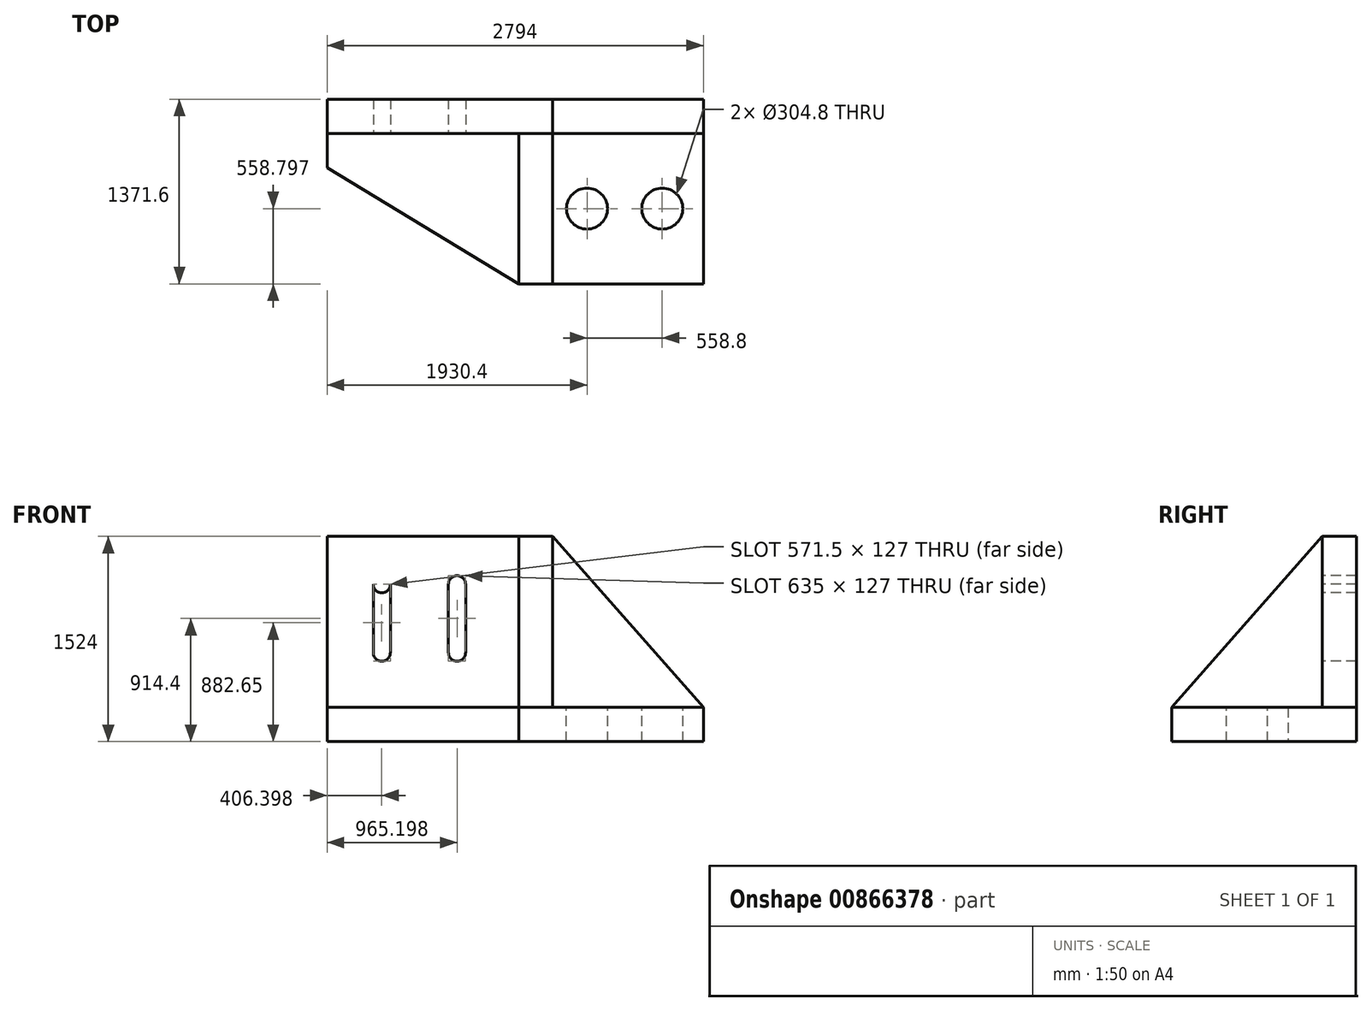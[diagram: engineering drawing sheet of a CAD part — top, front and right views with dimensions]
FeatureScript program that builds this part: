
annotation { "Feature Type Name" : "Feature", "Feature Type Description" : "" }
export const myFeature = defineFeature(function(context is Context, id is Id, definition is map)
    precondition{}
    {
        {
            var Q0;
            Q0=qCreatedBy(makeId("Top.planeOp"),FACE);
            var sketch = newSketch(context, id + "F0", { "sketchPlane" : qUnion([Q0])});
            skLineSegment(sketch, "E0", {"start": v(-275.52, -549.3) * mm, "end": v(1096.08, -549.3) * mm});
            skLineSegment(sketch, "E1", {"start": v(1096.08, -549.3) * mm, "end": v(1096.08, 822.3) * mm});
            skLineSegment(sketch, "E2", {"start": v(1096.08, 822.3) * mm, "end": v(-1697.92, 822.3) * mm});
            skLineSegment(sketch, "E3", {"start": v(-1697.92, 822.3) * mm, "end": v(-1697.92, 314.3) * mm});
            skLineSegment(sketch, "E4", {"start": v(-1697.92, 314.3) * mm, "end": v(-275.52, -549.3) * mm});
            skSolve(sketch);
        }
        {
            var Q0;
            Q0=makeQuery(id+"F0.imprint","IMPRINT",FACE,{"disambiguationData":[TD([[makeQuery(id+"F0.imprint","IMPRINT",EDGE,{"derivedFrom":sQuery(id+"F0.wireOp",EDGE,"E0")}),1.0]])]});
            extrude(context, id + "F1", {"entities" : qUnion([Q0]), "depth" : 254 * mm, "offsetDistance" : 25.4 * mm});
        }
        {
            var Q0;
            Q0=makeQuery(id+"F1.opExtrude","CAP_FACE",FACE,{"disambiguationData":[OSD([sQuery(id+"F0.wireOp",EDGE,"E0"),sQuery(id+"F0.wireOp",EDGE,"E1"),sQuery(id+"F0.wireOp",EDGE,"E2"),sQuery(id+"F0.wireOp",EDGE,"E3"),sQuery(id+"F0.wireOp",EDGE,"E4")])],"isStart":false});
            var sketch = newSketch(context, id + "F2", { "sketchPlane" : qUnion([Q0])});
            skLineSegment(sketch, "E5", {"start": v(-275.52, -549.3) * mm, "end": v(-275.52, 568.3) * mm});
            skLineSegment(sketch, "E6", {"start": v(-275.52, 568.3) * mm, "end": v(-1697.92, 568.3) * mm});
            skLineSegment(sketch, "E7", {"start": v(-21.52, -549.3) * mm, "end": v(-21.52, 568.3) * mm});
            skLineSegment(sketch, "E8", {"start": v(-21.52, 568.3) * mm, "end": v(1096.08, 568.3) * mm});
            skSolve(sketch);
        }
        {
            var Q0;
            {var subQ3=sQuery(id+"F2.wireOp",EDGE,"E5");Q0=makeQuery(id+"F2.imprint","IMPRINT",FACE,{"disambiguationData":[TD([[makeQuery(id+"F2.imprint","IMPRINT",EDGE,{"derivedFrom":subQ3}),-1.0]])]});}
            extrude(context, id + "F3", {"entities" : qUnion([Q0]), "operationType" : NewBodyOperationType.ADD, "depth" : 1270 * mm, "offsetDistance" : 25.4 * mm});
        }
        {
            var Q0;
            Q0=makeQuery(id+"F3.opExtrude","SWEPT_FACE",FACE,{"disambiguationData":[OSD([sQuery(id+"F2.wireOp",EDGE,"E8")])]});
            var sketch = newSketch(context, id + "F4", { "sketchPlane" : qUnion([Q0])});
            skLineSegment(sketch, "E9", {"start": v(-21.52, 1524) * mm, "end": v(1096.08, 254) * mm});
            skSolve(sketch);
        }
        {
            var Q0;
            Q0=makeQuery(id+"F4.imprint","IMPRINT",FACE,{"disambiguationData":[TD([[makeQuery(id+"F4.imprint","IMPRINT",EDGE,{"derivedFrom":sQuery(id+"F4.wireOp",EDGE,"E9")}),1.0]])]});
            extrude(context, id + "F5", {"entities" : qUnion([Q0]), "operationType" : NewBodyOperationType.REMOVE, "oppositeDirection" : true, "depth" : 701.04 * mm, "offsetDistance" : 25.4 * mm});
        }
        {
            var Q0;
            Q0=makeQuery(id+"F3.opExtrude","SWEPT_FACE",FACE,{"disambiguationData":[OSD([sQuery(id+"F2.wireOp",EDGE,"E7")])]});
            var sketch = newSketch(context, id + "F6", { "sketchPlane" : qUnion([Q0])});
            skLineSegment(sketch, "E10", {"start": v(568.3, 1524) * mm, "end": v(-549.3, 254) * mm});
            skSolve(sketch);
        }
        {
            var Q0;
            Q0=makeQuery(id+"F6.imprint","IMPRINT",FACE,{"disambiguationData":[TD([[makeQuery(id+"F6.imprint","IMPRINT",EDGE,{"derivedFrom":sQuery(id+"F6.wireOp",EDGE,"E10")}),-1.0]])]});
            extrude(context, id + "F7", {"entities" : qUnion([Q0]), "operationType" : NewBodyOperationType.REMOVE, "oppositeDirection" : true, "depth" : 2278.38 * mm, "offsetDistance" : 25.4 * mm});
        }
        {
            var Q0;
            Q0=makeQuery(id+"F3.opExtrude","SWEPT_FACE",FACE,{"disambiguationData":[OSD([sQuery(id+"F2.wireOp",EDGE,"E6")])]});
            var sketch = newSketch(context, id + "F8", { "sketchPlane" : qUnion([Q0])});
            skCircle(sketch, "E11", {"center": v(-1291.52, 1168.4) * mm, "radius": 63.5 * mm});
            skCircle(sketch, "E12", {"center": v(-1291.52, 660.4) * mm, "radius": 63.5 * mm});
            skCircle(sketch, "E13", {"center": v(-732.72, 1168.4) * mm, "radius": 63.5 * mm});
            skCircle(sketch, "E14", {"center": v(-732.72, 660.4) * mm, "radius": 63.5 * mm});
            skLineSegment(sketch, "E15", {"start": v(-1355.02, 1168.4) * mm, "end": v(-1355.02, 660.4) * mm});
            skLineSegment(sketch, "E16", {"start": v(-796.22, 1168.4) * mm, "end": v(-796.22, 660.4) * mm});
            skLineSegment(sketch, "E17", {"start": v(-1228.02, 660.4) * mm, "end": v(-1228.02, 1168.4) * mm});
            skLineSegment(sketch, "E18", {"start": v(-669.22, 1168.4) * mm, "end": v(-669.22, 660.4) * mm});
            skSolve(sketch);
        }
        {
            var Q0;
            {var subQ0=sQuery(id+"F8.wireOp",EDGE,"E11");var subQ2=makeQuery(id+"F8.imprint","IMPRINT",VERTEX,{"derivedFrom":subQ0});Q0=makeQuery(id+"F8.imprint","IMPRINT",FACE,{"disambiguationData":[TD([[makeQuery(id+"F8.imprint","IMPRINT",EDGE,{"disambiguationData":[TD([[subQ2,1.0]])],"derivedFrom":subQ0}),1.0]])]});}
            var Q1;
            {var subQ0=sQuery(id+"F8.wireOp",EDGE,"E15");Q1=makeQuery(id+"F8.imprint","IMPRINT",FACE,{"disambiguationData":[TD([[makeQuery(id+"F8.imprint","IMPRINT",EDGE,{"derivedFrom":subQ0}),1.0]])]});}
            var Q2;
            {var subQ0=sQuery(id+"F8.wireOp",EDGE,"E12");var subQ1=makeQuery(id+"F8.imprint","INTERSECT",VERTEX,{"derivedFrom":[subQ0,sQuery(id+"F8.wireOp",EDGE,"E15")]});Q2=makeQuery(id+"F8.imprint","IMPRINT",FACE,{"disambiguationData":[TD([[makeQuery(id+"F8.imprint","IMPRINT",EDGE,{"disambiguationData":[TD([[subQ1,1.0]])],"derivedFrom":subQ0}),1.0]])]});}
            var Q3;
            {var subQ0=sQuery(id+"F8.wireOp",EDGE,"E13");var subQ1=makeQuery(id+"F8.imprint","INTERSECT",VERTEX,{"derivedFrom":[subQ0,sQuery(id+"F8.wireOp",EDGE,"E16")]});Q3=makeQuery(id+"F8.imprint","IMPRINT",FACE,{"disambiguationData":[TD([[makeQuery(id+"F8.imprint","IMPRINT",EDGE,{"disambiguationData":[TD([[subQ1,1.0]])],"derivedFrom":subQ0}),1.0]])]});}
            var Q4;
            {var subQ0=sQuery(id+"F8.wireOp",EDGE,"E16");Q4=makeQuery(id+"F8.imprint","IMPRINT",FACE,{"disambiguationData":[TD([[makeQuery(id+"F8.imprint","IMPRINT",EDGE,{"derivedFrom":subQ0}),1.0]])]});}
            var Q5;
            {var subQ0=sQuery(id+"F8.wireOp",EDGE,"E14");var subQ1=makeQuery(id+"F8.imprint","INTERSECT",VERTEX,{"derivedFrom":[subQ0,sQuery(id+"F8.wireOp",EDGE,"E16")]});Q5=makeQuery(id+"F8.imprint","IMPRINT",FACE,{"disambiguationData":[TD([[makeQuery(id+"F8.imprint","IMPRINT",EDGE,{"disambiguationData":[TD([[subQ1,1.0]])],"derivedFrom":subQ0}),1.0]])]});}
            extrude(context, id + "F9", {"entities" : qUnion([Q0, Q1, Q2, Q3, Q4, Q5]), "operationType" : NewBodyOperationType.REMOVE, "oppositeDirection" : true, "depth" : 584.2 * mm, "offsetDistance" : 25.4 * mm});
        }
        {
            var Q0;
            {var subQ0=sQuery(id+"F0.wireOp",EDGE,"E1");var subQ1=sQuery(id+"F0.wireOp",EDGE,"E0");Q0=makeQuery(id+"F3.boolean.opBoolean","SPLIT",FACE,{"disambiguationData":[TD([makeQuery(id+"F1.opExtrude","SWEPT_FACE",FACE,{"disambiguationData":[OSD([subQ0])]})])],"derivedFrom":makeQuery(id+"F1.opExtrude","CAP_FACE",FACE,{"disambiguationData":[OSD([subQ1,subQ0,sQuery(id+"F0.wireOp",EDGE,"E2"),sQuery(id+"F0.wireOp",EDGE,"E3"),sQuery(id+"F0.wireOp",EDGE,"E4")])],"isStart":false})});}
            var sketch = newSketch(context, id + "F10", { "sketchPlane" : qUnion([Q0])});
            skCircle(sketch, "E19", {"center": v(791.28, 9.5) * mm, "radius": 152.4 * mm});
            skCircle(sketch, "E20", {"center": v(232.48, 9.5) * mm, "radius": 152.4 * mm});
            skSolve(sketch);
        }
        {
            var Q0;
            Q0=makeQuery(id+"F10.imprint","IMPRINT",FACE,{"disambiguationData":[TD([[makeQuery(id+"F10.imprint","IMPRINT",EDGE,{"derivedFrom":sQuery(id+"F10.wireOp",EDGE,"E20")}),1.0]])]});
            var Q1;
            Q1=makeQuery(id+"F10.imprint","IMPRINT",FACE,{"disambiguationData":[TD([[makeQuery(id+"F10.imprint","IMPRINT",EDGE,{"derivedFrom":sQuery(id+"F10.wireOp",EDGE,"E19")}),1.0]])]});
            extrude(context, id + "F11", {"entities" : qUnion([Q0, Q1]), "operationType" : NewBodyOperationType.REMOVE, "oppositeDirection" : true, "depth" : 1562.1 * mm, "offsetDistance" : 25.4 * mm});
        }
    });
